# Revit family: C224-30-S-1
name_source: partatom
category: Plumbing Fixtures
units: mm (PartAtom-declared; Revit-internal decimal feet)

## family parameters
Cut with Voids When Loaded = No
Enable Cutting in Views = No
Host = Face
Maintain Annotation Orientation = No
Part Type = Normal
Room Calculation Point = No
Round Connector Dimension = Use Radius
Shared = No

## types (3) — shared parameters
Body Height = 4.4 "
Description = 5” SQUARE ADJUSTABLE FLOOR CLEANOUT
Floor Drain Material = Paint - Sherwin Williams Paint - #952C2A - Bellwood Red
Manufacturer = MIFAB
Top Assembly Adjustment = 1.5 "
URL = WWW.MIFAB.COM
zero-valued in all types: CWFU, Default Elevation, WFU

## per-type parameters (varying)
| type | Model | Pipe Diameter | Pipe Radius |
| C224-30-S-1_Pipe Size 2" | C220-S | 2 " | 1 " |
| C224-30-S-1_Pipe Size 3" | C220-S | 3 " | 1.5 " |
| C224-30-S-1_Pipe Size 4" | C224-30-S-1 | 4 " | 2 " |

## geometry (parser evidence)
native form markers: Blend x2, Sweep x2
no freeform markers — native parametric forms only
